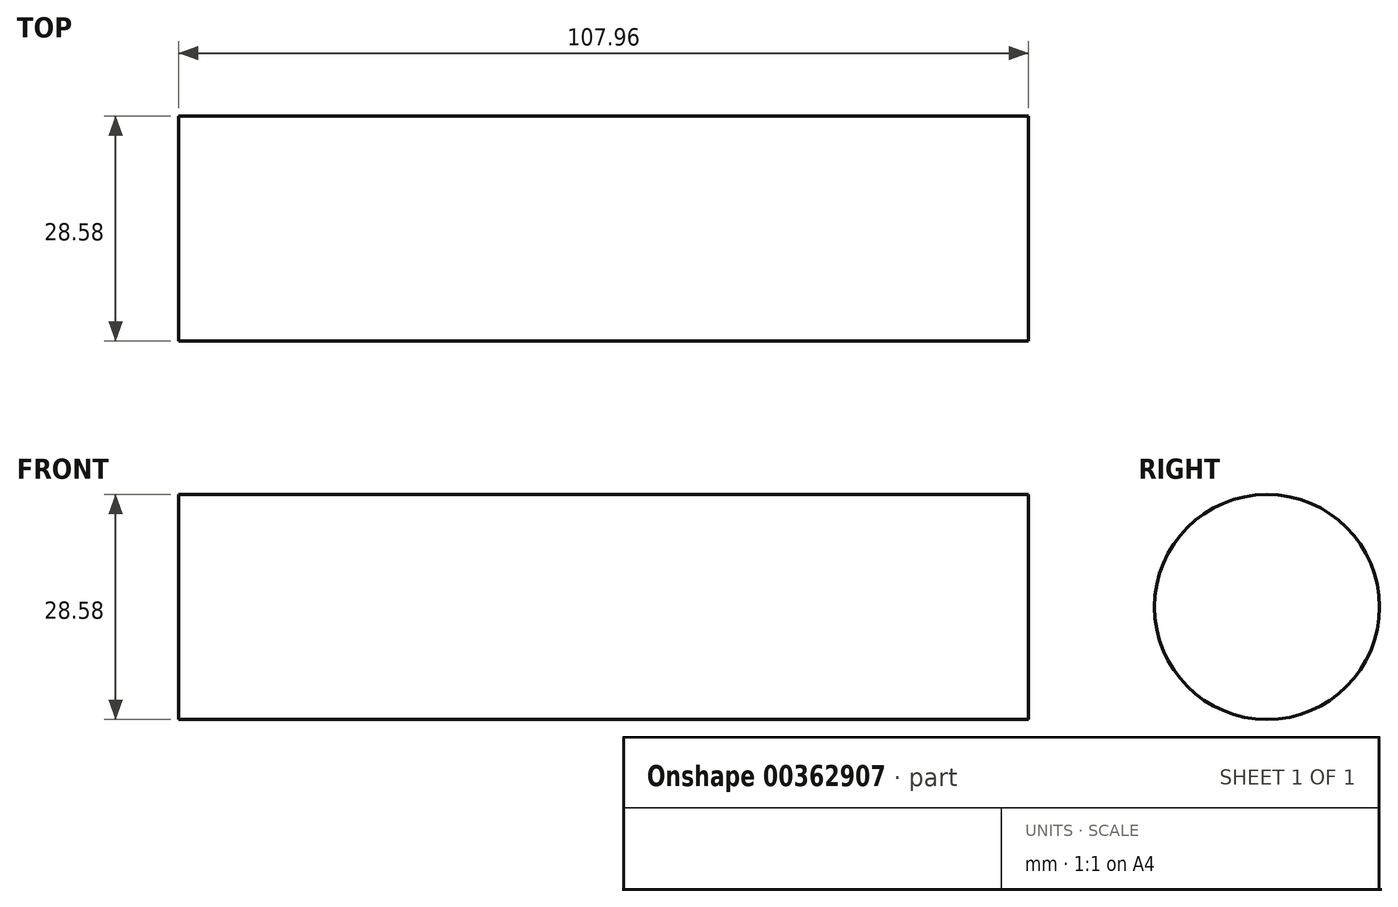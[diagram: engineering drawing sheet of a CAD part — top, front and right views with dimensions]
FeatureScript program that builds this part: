
annotation { "Feature Type Name" : "Feature", "Feature Type Description" : "" }
export const myFeature = defineFeature(function(context is Context, id is Id, definition is map)
    precondition{}
    {
        {
            var Q0;
            Q0=qCreatedBy(makeId("Right.planeOp"),FACE);
            var sketch = newSketch(context, id + "F0", { "sketchPlane" : qUnion([Q0])});
            skCircle(sketch, "E0", {"center": v(0, 0) * mm, "radius": 14.29 * mm});
            skSolve(sketch);
        }
        {
            var Q0;
            Q0=makeQuery(id+"F0.imprint","IMPRINT",FACE,{"disambiguationData":[TD([[makeQuery(id+"F0.imprint","IMPRINT",EDGE,{"derivedFrom":sQuery(id+"F0.wireOp",EDGE,"E0")}),1.0]])]});
            extrude(context, id + "F1", {"entities" : qUnion([Q0]), "depth" : 53.97 * mm, "hasSecondDirection" : true, "secondDirectionOppositeDirection" : true, "secondDirectionDepth" : 53.97 * mm});
        }
    });
